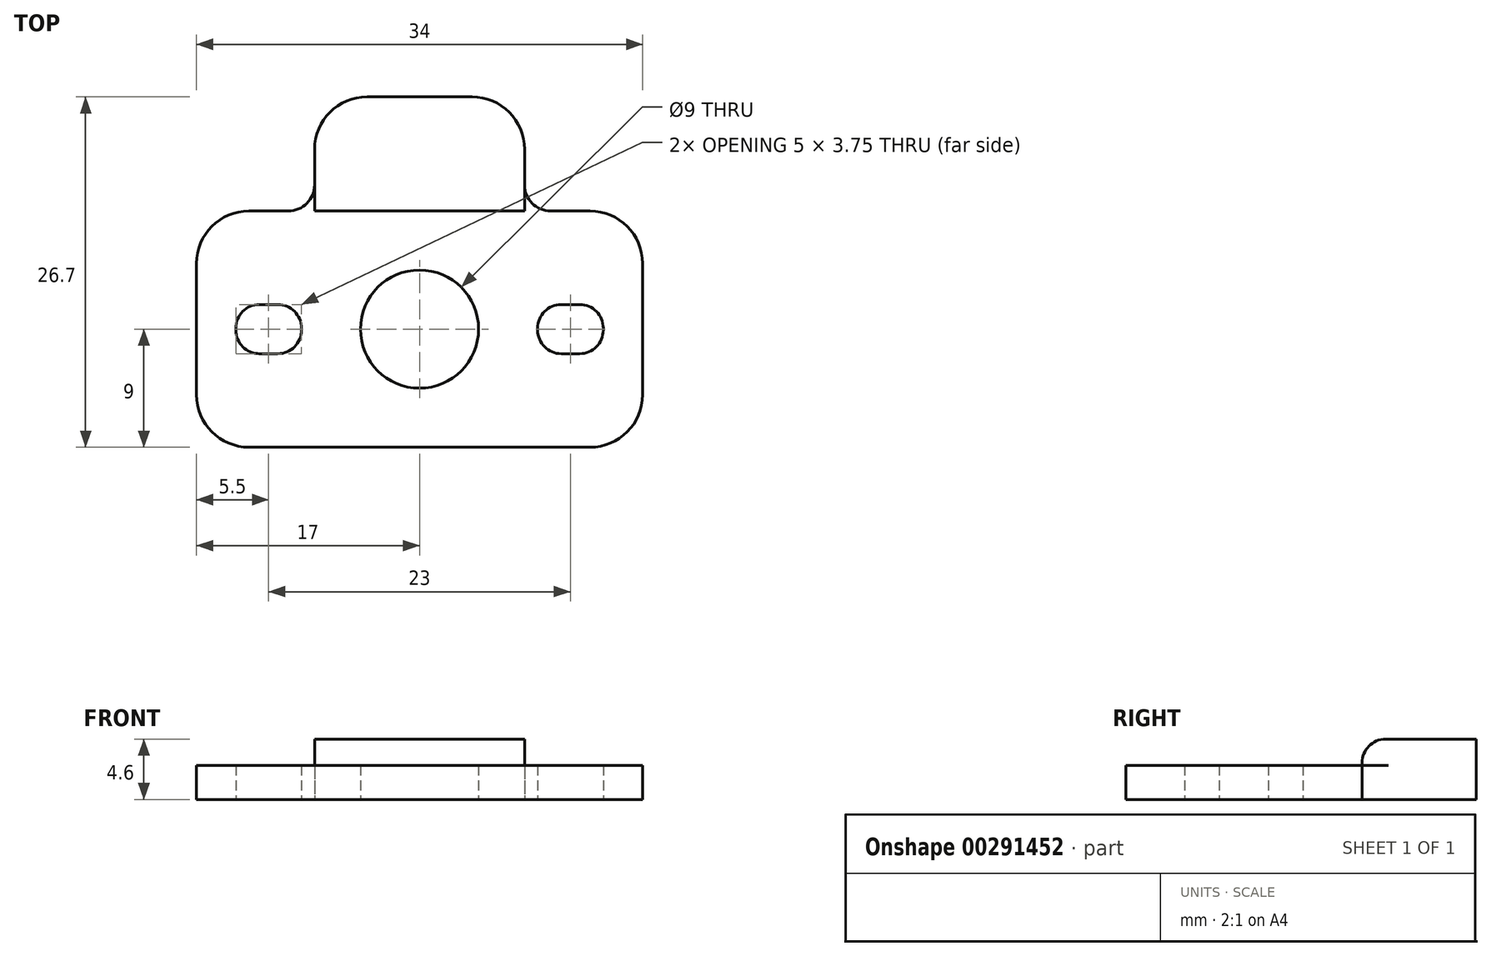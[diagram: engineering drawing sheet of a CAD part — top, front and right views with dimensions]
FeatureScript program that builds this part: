
annotation { "Feature Type Name" : "Feature", "Feature Type Description" : "" }
export const myFeature = defineFeature(function(context is Context, id is Id, definition is map)
    precondition{}
    {
        {
            var Q0;
            Q0=qCreatedBy(makeId("Top.planeOp"),FACE);
            var sketch = newSketch(context, id + "F0", { "sketchPlane" : qUnion([Q0])});
            skLineSegment(sketch, "E0.bottom", {"start": v(17, 9) * mm, "end": v(8, 9) * mm});
            skLineSegment(sketch, "E0.top", {"start": v(17, -9) * mm, "end": v(-17, -9) * mm});
            skLineSegment(sketch, "E0.left", {"start": v(17, 9) * mm, "end": v(17, -9) * mm});
            skLineSegment(sketch, "E0.right", {"start": v(-17, 9) * mm, "end": v(-17, -9) * mm});
            skPoint(sketch, "E0.middle", {"position": v(0, 0) * mm});
            skLineSegment(sketch, "E1", {"start": v(-8, 9) * mm, "end": v(-8, 17.7) * mm});
            skLineSegment(sketch, "E2", {"start": v(-8, 17.7) * mm, "end": v(8, 17.7) * mm});
            skLineSegment(sketch, "E3", {"start": v(8, 17.7) * mm, "end": v(8, 9) * mm});
            skLineSegment(sketch, "E4.trimOffspring", {"start": v(-8, 9) * mm, "end": v(-17, 9) * mm});
            skCircle(sketch, "E5", {"center": v(0, 0) * mm, "radius": 4.5 * mm});
            skLineSegment(sketch, "E6.bottom", {"start": v(-9, -1.88) * mm, "end": v(-14, -1.88) * mm});
            skLineSegment(sketch, "E6.top", {"start": v(-9, 1.87) * mm, "end": v(-14, 1.87) * mm});
            skLineSegment(sketch, "E6.left", {"start": v(-9, -1.88) * mm, "end": v(-9, 1.87) * mm});
            skLineSegment(sketch, "E6.right", {"start": v(-14, -1.88) * mm, "end": v(-14, 1.87) * mm});
            skPoint(sketch, "E6.middle", {"position": v(-11.5, 0) * mm});
            skLineSegment(sketch, "E7.bottom", {"start": v(14, -1.87) * mm, "end": v(9, -1.87) * mm});
            skLineSegment(sketch, "E7.top", {"start": v(14, 1.88) * mm, "end": v(9, 1.88) * mm});
            skLineSegment(sketch, "E7.left", {"start": v(14, -1.87) * mm, "end": v(14, 1.88) * mm});
            skLineSegment(sketch, "E7.right", {"start": v(9, -1.87) * mm, "end": v(9, 1.88) * mm});
            skPoint(sketch, "E7.middle", {"position": v(11.5, 0) * mm});
            skSolve(sketch);
        }
        {
            var Q0;
            Q0=makeQuery(id+"F0.imprint","IMPRINT",FACE,{"disambiguationData":[TD([[makeQuery(id+"F0.imprint","IMPRINT",EDGE,{"derivedFrom":sQuery(id+"F0.wireOp",EDGE,"E0.bottom")}),1.0]])]});
            extrude(context, id + "F1", {"entities" : qUnion([Q0]), "depth" : 2.6 * mm});
        }
        {
            var Q0;
            Q0=makeQuery(id+"F1.opExtrude","CAP_FACE",FACE,{"disambiguationData":[OSD([sQuery(id+"F0.wireOp",EDGE,"E0.bottom"),sQuery(id+"F0.wireOp",EDGE,"E0.top"),sQuery(id+"F0.wireOp",EDGE,"E0.left"),sQuery(id+"F0.wireOp",EDGE,"E0.right"),sQuery(id+"F0.wireOp",EDGE,"E1"),sQuery(id+"F0.wireOp",EDGE,"E2"),sQuery(id+"F0.wireOp",EDGE,"E3"),sQuery(id+"F0.wireOp",EDGE,"E4.trimOffspring"),sQuery(id+"F0.wireOp",EDGE,"E5"),sQuery(id+"F0.wireOp",EDGE,"E6.bottom"),sQuery(id+"F0.wireOp",EDGE,"E6.top"),sQuery(id+"F0.wireOp",EDGE,"E6.left"),sQuery(id+"F0.wireOp",EDGE,"E6.right"),sQuery(id+"F0.wireOp",EDGE,"E7.bottom"),sQuery(id+"F0.wireOp",EDGE,"E7.top"),sQuery(id+"F0.wireOp",EDGE,"E7.left"),sQuery(id+"F0.wireOp",EDGE,"E7.right")])],"isStart":false});
            var sketch = newSketch(context, id + "F2", { "sketchPlane" : qUnion([Q0])});
            skLineSegment(sketch, "E8.bottom", {"start": v(-8, 17.7) * mm, "end": v(8, 17.7) * mm});
            skLineSegment(sketch, "E8.top", {"start": v(-8, 9) * mm, "end": v(8, 9) * mm});
            skLineSegment(sketch, "E8.left", {"start": v(-8, 17.7) * mm, "end": v(-8, 9) * mm});
            skLineSegment(sketch, "E8.right", {"start": v(8, 17.7) * mm, "end": v(8, 9) * mm});
            skSolve(sketch);
        }
        {
            var Q0;
            Q0=makeQuery(id+"F2.imprint","IMPRINT",FACE,{"disambiguationData":[TD([[makeQuery(id+"F2.imprint","IMPRINT",EDGE,{"derivedFrom":sQuery(id+"F2.wireOp",EDGE,"E8.bottom")}),-1.0]])]});
            extrude(context, id + "F3", {"entities" : qUnion([Q0]), "operationType" : NewBodyOperationType.ADD, "depth" : 2 * mm});
        }
        {
            var Q0;
            Q0=makeQuery(id+"F1.opExtrude","SWEPT_EDGE",EDGE,{"disambiguationData":[OSD([sQuery(id+"F0.wireOp",EDGE,"E0.bottom"),sQuery(id+"F0.wireOp",EDGE,"E0.left")])]});
            var Q1;
            Q1=makeQuery(id+"F1.opExtrude","SWEPT_EDGE",EDGE,{"disambiguationData":[OSD([sQuery(id+"F0.wireOp",EDGE,"E0.top"),sQuery(id+"F0.wireOp",EDGE,"E0.left")])]});
            var Q2;
            Q2=makeQuery(id+"F1.opExtrude","SWEPT_EDGE",EDGE,{"disambiguationData":[OSD([sQuery(id+"F0.wireOp",EDGE,"E0.right"),sQuery(id+"F0.wireOp",EDGE,"E4.trimOffspring")])]});
            var Q3;
            Q3=makeQuery(id+"F1.opExtrude","SWEPT_EDGE",EDGE,{"disambiguationData":[OSD([sQuery(id+"F0.wireOp",EDGE,"E0.top"),sQuery(id+"F0.wireOp",EDGE,"E0.right")])]});
            var Q4;
            Q4=makeQuery(id+"F3.boolean.opBoolean","MERGE",EDGE,{"derivedFrom":[makeQuery(id+"F1.opExtrude","SWEPT_EDGE",EDGE,{"disambiguationData":[OSD([sQuery(id+"F0.wireOp",EDGE,"E2"),sQuery(id+"F0.wireOp",EDGE,"E3")])]}),makeQuery(id+"F3.opExtrude","SWEPT_EDGE",EDGE,{"disambiguationData":[OSD([sQuery(id+"F2.wireOp",EDGE,"E8.bottom"),sQuery(id+"F2.wireOp",EDGE,"E8.right")])]})]});
            var Q5;
            Q5=makeQuery(id+"F3.boolean.opBoolean","MERGE",EDGE,{"derivedFrom":[makeQuery(id+"F1.opExtrude","SWEPT_EDGE",EDGE,{"disambiguationData":[OSD([sQuery(id+"F0.wireOp",EDGE,"E1"),sQuery(id+"F0.wireOp",EDGE,"E2")])]}),makeQuery(id+"F3.opExtrude","SWEPT_EDGE",EDGE,{"disambiguationData":[OSD([sQuery(id+"F2.wireOp",EDGE,"E8.bottom"),sQuery(id+"F2.wireOp",EDGE,"E8.left")])]})]});
            fillet(context, id + "F4", {"entities" : qUnion([Q0, Q1, Q2, Q3, Q4, Q5]), "radius" : 4 * mm, "tangentPropagation" : true, "allowEdgeOverflow" : false});
        }
        {
            var Q0;
            Q0=makeQuery(id+"F3.opExtrude","CAP_EDGE",EDGE,{"disambiguationData":[OSD([sQuery(id+"F2.wireOp",EDGE,"E8.top")])],"isStart":false});
            var Q1;
            Q1=makeQuery(id+"F1.opExtrude","SWEPT_EDGE",EDGE,{"disambiguationData":[OSD([sQuery(id+"F0.wireOp",EDGE,"E6.top"),sQuery(id+"F0.wireOp",EDGE,"E6.right")])]});
            var Q2;
            Q2=makeQuery(id+"F1.opExtrude","SWEPT_EDGE",EDGE,{"disambiguationData":[OSD([sQuery(id+"F0.wireOp",EDGE,"E6.bottom"),sQuery(id+"F0.wireOp",EDGE,"E6.right")])]});
            var Q3;
            Q3=makeQuery(id+"F1.opExtrude","SWEPT_EDGE",EDGE,{"disambiguationData":[OSD([sQuery(id+"F0.wireOp",EDGE,"E6.top"),sQuery(id+"F0.wireOp",EDGE,"E6.left")])]});
            var Q4;
            Q4=makeQuery(id+"F1.opExtrude","SWEPT_EDGE",EDGE,{"disambiguationData":[OSD([sQuery(id+"F0.wireOp",EDGE,"E6.bottom"),sQuery(id+"F0.wireOp",EDGE,"E6.left")])]});
            var Q5;
            Q5=makeQuery(id+"F1.opExtrude","SWEPT_EDGE",EDGE,{"disambiguationData":[OSD([sQuery(id+"F0.wireOp",EDGE,"E7.top"),sQuery(id+"F0.wireOp",EDGE,"E7.left")])]});
            var Q6;
            Q6=makeQuery(id+"F1.opExtrude","SWEPT_EDGE",EDGE,{"disambiguationData":[OSD([sQuery(id+"F0.wireOp",EDGE,"E7.top"),sQuery(id+"F0.wireOp",EDGE,"E7.right")])]});
            var Q7;
            Q7=makeQuery(id+"F1.opExtrude","SWEPT_EDGE",EDGE,{"disambiguationData":[OSD([sQuery(id+"F0.wireOp",EDGE,"E7.bottom"),sQuery(id+"F0.wireOp",EDGE,"E7.right")])]});
            var Q8;
            Q8=makeQuery(id+"F1.opExtrude","SWEPT_EDGE",EDGE,{"disambiguationData":[OSD([sQuery(id+"F0.wireOp",EDGE,"E7.bottom"),sQuery(id+"F0.wireOp",EDGE,"E7.left")])]});
            fillet(context, id + "F5", {"entities" : qUnion([Q0, Q1, Q2, Q3, Q4, Q5, Q6, Q7, Q8]), "radius" : 1.8 * mm, "tangentPropagation" : true, "allowEdgeOverflow" : false});
        }
        {
            var Q0;
            Q0=makeQuery(id+"F1.opExtrude","SWEPT_EDGE",EDGE,{"disambiguationData":[OSD([sQuery(id+"F0.wireOp",EDGE,"E0.bottom"),sQuery(id+"F0.wireOp",EDGE,"E3")])]});
            var Q1;
            Q1=makeQuery(id+"F1.opExtrude","SWEPT_EDGE",EDGE,{"disambiguationData":[OSD([sQuery(id+"F0.wireOp",EDGE,"E1"),sQuery(id+"F0.wireOp",EDGE,"E4.trimOffspring")])]});
            fillet(context, id + "F6", {"entities" : qUnion([Q0, Q1]), "radius" : 2 * mm, "tangentPropagation" : true, "allowEdgeOverflow" : false});
        }
    });
